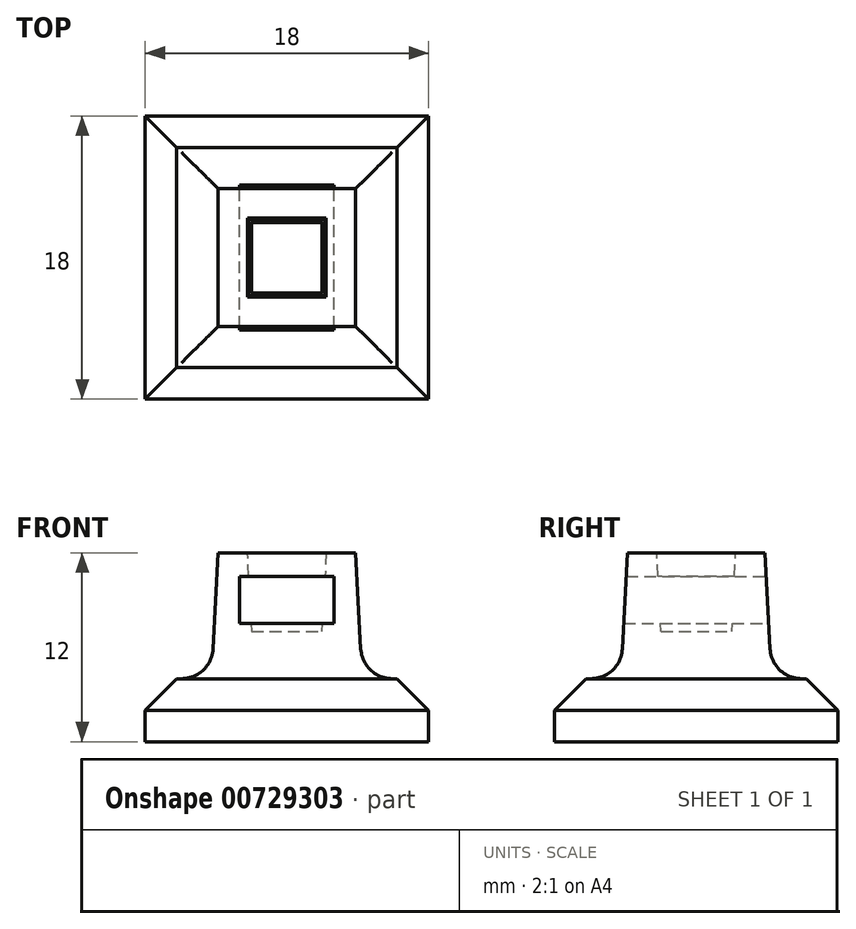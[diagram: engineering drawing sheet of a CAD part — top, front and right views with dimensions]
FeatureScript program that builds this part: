
annotation { "Feature Type Name" : "Feature", "Feature Type Description" : "" }
export const myFeature = defineFeature(function(context is Context, id is Id, definition is map)
    precondition{}
    {
        {
            var Q0;
            Q0=qCreatedBy(makeId("Top.planeOp"),FACE);
            var sketch = newSketch(context, id + "F0", { "sketchPlane" : qUnion([Q0])});
            skLineSegment(sketch, "E0.bottom", {"start": v(-9, 9) * mm, "end": v(9, 9) * mm});
            skLineSegment(sketch, "E0.top", {"start": v(-9, -9) * mm, "end": v(9, -9) * mm});
            skLineSegment(sketch, "E0.left", {"start": v(-9, 9) * mm, "end": v(-9, -9) * mm});
            skLineSegment(sketch, "E0.right", {"start": v(9, 9) * mm, "end": v(9, -9) * mm});
            skPoint(sketch, "E0.middle", {"position": v(0, 0) * mm});
            skLineSegment(sketch, "E1.bottom", {"start": v(5, -5) * mm, "end": v(-5, -5) * mm});
            skLineSegment(sketch, "E1.top", {"start": v(5, 5) * mm, "end": v(-5, 5) * mm});
            skLineSegment(sketch, "E1.left", {"start": v(5, -5) * mm, "end": v(5, 5) * mm});
            skLineSegment(sketch, "E1.right", {"start": v(-5, -5) * mm, "end": v(-5, 5) * mm});
            skSolve(sketch);
        }
        {
            var Q0;
            Q0=makeQuery(id+"F0.imprint","IMPRINT",FACE,{"disambiguationData":[TD([[makeQuery(id+"F0.imprint","IMPRINT",EDGE,{"derivedFrom":sQuery(id+"F0.wireOp",EDGE,"E0.bottom")}),-1.0]])]});
            var Q1;
            Q1=makeQuery(id+"F0.imprint","IMPRINT",FACE,{"disambiguationData":[TD([[makeQuery(id+"F0.imprint","IMPRINT",EDGE,{"derivedFrom":sQuery(id+"F0.wireOp",EDGE,"E1.bottom")}),-1.0]])]});
            extrude(context, id + "F1", {"entities" : qUnion([Q0, Q1]), "depth" : 4 * mm, "offsetDistance" : 25 * mm});
        }
        {
            var Q0;
            Q0=makeQuery(id+"F0.imprint","IMPRINT",FACE,{"disambiguationData":[TD([[makeQuery(id+"F0.imprint","IMPRINT",EDGE,{"derivedFrom":sQuery(id+"F0.wireOp",EDGE,"E1.bottom")}),-1.0]])]});
            extrude(context, id + "F2", {"entities" : qUnion([Q0]), "operationType" : NewBodyOperationType.ADD, "depth" : 12 * mm, "offsetDistance" : 25 * mm, "hasDraft" : true, "draftAngle" : 3 * degree, "draftPullDirection" : true});
        }
        {
            var Q0;
            Q0=makeQuery(id+"F1.opExtrude","CAP_EDGE",EDGE,{"disambiguationData":[OSD([sQuery(id+"F0.wireOp",EDGE,"E0.left")])],"isStart":false});
            var Q1;
            Q1=makeQuery(id+"F1.opExtrude","CAP_EDGE",EDGE,{"disambiguationData":[OSD([sQuery(id+"F0.wireOp",EDGE,"E0.top")])],"isStart":false});
            var Q2;
            Q2=makeQuery(id+"F1.opExtrude","CAP_EDGE",EDGE,{"disambiguationData":[OSD([sQuery(id+"F0.wireOp",EDGE,"E0.right")])],"isStart":false});
            var Q3;
            Q3=makeQuery(id+"F1.opExtrude","CAP_EDGE",EDGE,{"disambiguationData":[OSD([sQuery(id+"F0.wireOp",EDGE,"E0.bottom")])],"isStart":false});
            chamfer(context, id + "F3", {"entities" : qUnion([Q0, Q1, Q2, Q3]), "width" : 2 * mm, "tangentPropagation" : true});
        }
        {
            var Q0;
            Q0=makeQuery(id+"F2.boolean.opBoolean","INTERSECT",EDGE,{"derivedFrom":[makeQuery(id+"F1.opExtrude","CAP_FACE",FACE,{"disambiguationData":[OSD([sQuery(id+"F0.wireOp",EDGE,"E0.bottom"),sQuery(id+"F0.wireOp",EDGE,"E0.top"),sQuery(id+"F0.wireOp",EDGE,"E0.left"),sQuery(id+"F0.wireOp",EDGE,"E0.right")])],"isStart":false}),makeQuery(id+"F2.opExtrude","SWEPT_FACE",FACE,{"disambiguationData":[OSD([sQuery(id+"F0.wireOp",EDGE,"E1.bottom")])]})]});
            var Q1;
            Q1=makeQuery(id+"F2.boolean.opBoolean","INTERSECT",EDGE,{"derivedFrom":[makeQuery(id+"F1.opExtrude","CAP_FACE",FACE,{"disambiguationData":[OSD([sQuery(id+"F0.wireOp",EDGE,"E0.bottom"),sQuery(id+"F0.wireOp",EDGE,"E0.top"),sQuery(id+"F0.wireOp",EDGE,"E0.left"),sQuery(id+"F0.wireOp",EDGE,"E0.right")])],"isStart":false}),makeQuery(id+"F2.opExtrude","SWEPT_FACE",FACE,{"disambiguationData":[OSD([sQuery(id+"F0.wireOp",EDGE,"E1.right")])]})]});
            var Q2;
            Q2=makeQuery(id+"F2.boolean.opBoolean","INTERSECT",EDGE,{"derivedFrom":[makeQuery(id+"F1.opExtrude","CAP_FACE",FACE,{"disambiguationData":[OSD([sQuery(id+"F0.wireOp",EDGE,"E0.bottom"),sQuery(id+"F0.wireOp",EDGE,"E0.top"),sQuery(id+"F0.wireOp",EDGE,"E0.left"),sQuery(id+"F0.wireOp",EDGE,"E0.right")])],"isStart":false}),makeQuery(id+"F2.opExtrude","SWEPT_FACE",FACE,{"disambiguationData":[OSD([sQuery(id+"F0.wireOp",EDGE,"E1.left")])]})]});
            var Q3;
            Q3=makeQuery(id+"F2.boolean.opBoolean","INTERSECT",EDGE,{"derivedFrom":[makeQuery(id+"F1.opExtrude","CAP_FACE",FACE,{"disambiguationData":[OSD([sQuery(id+"F0.wireOp",EDGE,"E0.bottom"),sQuery(id+"F0.wireOp",EDGE,"E0.top"),sQuery(id+"F0.wireOp",EDGE,"E0.left"),sQuery(id+"F0.wireOp",EDGE,"E0.right")])],"isStart":false}),makeQuery(id+"F2.opExtrude","SWEPT_FACE",FACE,{"disambiguationData":[OSD([sQuery(id+"F0.wireOp",EDGE,"E1.top")])]})]});
            fillet(context, id + "F4", {"entities" : qUnion([Q0, Q1, Q2, Q3]), "radius" : 2 * mm, "tangentPropagation" : true, "allowEdgeOverflow" : false});
        }
        {
            var Q0;
            Q0=makeQuery(id+"F2.opExtrude","CAP_FACE",FACE,{"disambiguationData":[OSD([sQuery(id+"F0.wireOp",EDGE,"E1.bottom"),sQuery(id+"F0.wireOp",EDGE,"E1.top"),sQuery(id+"F0.wireOp",EDGE,"E1.left"),sQuery(id+"F0.wireOp",EDGE,"E1.right")])],"isStart":false});
            var sketch = newSketch(context, id + "F5", { "sketchPlane" : qUnion([Q0])});
            skLineSegment(sketch, "E2.bottom", {"start": v(2.5, -2.5) * mm, "end": v(-2.5, -2.5) * mm});
            skLineSegment(sketch, "E2.top", {"start": v(2.5, 2.5) * mm, "end": v(-2.5, 2.5) * mm});
            skLineSegment(sketch, "E2.left", {"start": v(2.5, -2.5) * mm, "end": v(2.5, 2.5) * mm});
            skLineSegment(sketch, "E2.right", {"start": v(-2.5, -2.5) * mm, "end": v(-2.5, 2.5) * mm});
            skPoint(sketch, "E2.middle", {"position": v(0, 0) * mm});
            skSolve(sketch);
        }
        {
            var Q0;
            Q0 = qSketchRegion(id + "F5", true);
            extrude(context, id + "F6", {"entities" : qUnion([Q0]), "operationType" : NewBodyOperationType.REMOVE, "oppositeDirection" : true, "depth" : 5 * mm, "offsetDistance" : 25 * mm, "hasDraft" : true, "draftAngle" : 3 * degree, "draftPullDirection" : true});
        }
        {
            var Q0;
            Q0=qCreatedBy(makeId("Front.planeOp"),FACE);
            var sketch = newSketch(context, id + "F7", { "sketchPlane" : qUnion([Q0])});
            skLineSegment(sketch, "E3", {"start": v(0, 0) * mm, "end": v(0, 9) * mm, "construction": true});
            skLineSegment(sketch, "E4.bottom", {"start": v(-3, 7.5) * mm, "end": v(3, 7.5) * mm});
            skLineSegment(sketch, "E4.top", {"start": v(-3, 10.5) * mm, "end": v(3, 10.5) * mm});
            skLineSegment(sketch, "E4.left", {"start": v(-3, 7.5) * mm, "end": v(-3, 10.5) * mm});
            skLineSegment(sketch, "E4.right", {"start": v(3, 7.5) * mm, "end": v(3, 10.5) * mm});
            skPoint(sketch, "E4.middle", {"position": v(0, 9) * mm});
            skSolve(sketch);
        }
        {
            var Q0;
            Q0 = qSketchRegion(id + "F7", true);
            extrude(context, id + "F8", {"entities" : qUnion([Q0]), "operationType" : NewBodyOperationType.REMOVE, "depth" : 25 * mm, "offsetDistance" : 25 * mm, "hasSecondDirection" : true, "secondDirectionOppositeDirection" : true, "secondDirectionDepth" : 25 * mm});
        }
    });
